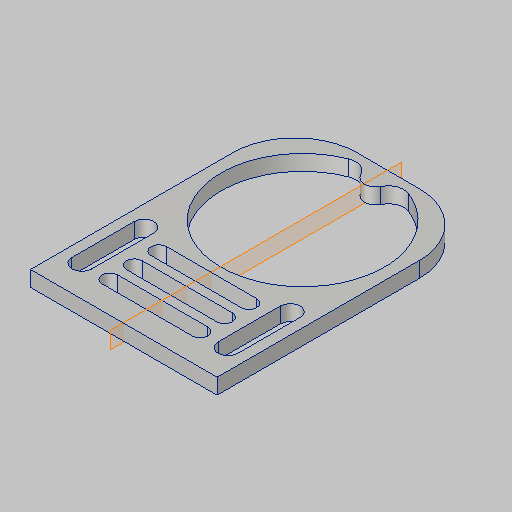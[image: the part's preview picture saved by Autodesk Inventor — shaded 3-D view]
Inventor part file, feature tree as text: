
AUTODESK INVENTOR PART (.ipt)
format: ipt  version: 2023.5 (Build 275446000, 446)  size: 173,568 bytes
history: native  units: in
note: dims shown in document units (in); Inventor stores cm internally (conversion verified against a paired STEP export)
features: extrude x2, fillet x2, sketch x2
ambient origin geometry x8: Origin, YZ Plane, XZ Plane, XY Plane, X Axis, Y Axis, Z Axis, Center Point
bodies: Solid1 (feature_tree)
feature tree (6):
  extrude  "Extrusion1"  Depth=0.125in
  extrude  "Extrusion2"  Depth=0.1969in
  fillet  "Fillet1"  Radius=1.5in
  fillet  "Fillet2"  Radius=2.125in
  sketch  "Sketch1"  dims[d0=0.725in d1=0.125in]
  sketch  "Sketch2"  dims[d6=0.1969in d7=0.1969in d8=1.5in d9=2.125in d10=0.25in d11=1.3125in d12=0.125in d13=0.0in d14=0.18in d15=0.1in d16=0.125in d17=0.0in d18=0.125in d19=0.5in d20=0.6875in d21=0.159in d22=0.159in d23=0.5in d26=0.5in]
